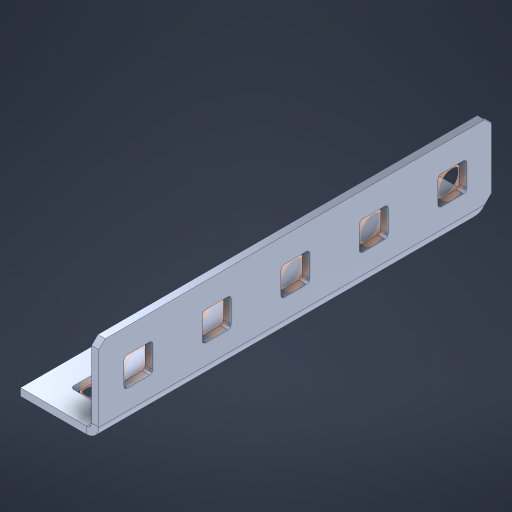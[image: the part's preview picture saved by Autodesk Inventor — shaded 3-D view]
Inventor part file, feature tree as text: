
AUTODESK INVENTOR PART (.ipt)
format: ipt  version: 2023 (Build 270158000, 158)  size: 450,560 bytes
history: native  units: in
note: dims shown in document units (in); Inventor stores cm internally (conversion verified against a paired STEP export)
features: other x15, sheet_metal_op x10, extrude x9, sketch x8, mirror x1, pattern_linear x1, chamfer x1
ambient origin geometry x8: Origin, YZ Plane, XZ Plane, XY Plane, X Axis, Y Axis, Z Axis, Center Point
bodies: Solid1 (feature_tree), Body (feature_tree)
feature tree (45):
  other  "Flange Pattern Plane"
  sheet_metal_op  "Flange Pattern"
  sheet_metal_op  "Body Pattern"
  other  "Arc Length"
  mirror  "Notch Mirror"
  pattern_linear  "Notch Pattern"  Spacing1=0.1875in  [1 undecoded]
  chamfer  "End Chamfer"
  extrude  "Half Cut"  Depth=0.0469in
  sketch  "Sketch1"  dims[d0=2.5in]
  other  "Plate1"
  sketch  "Sketch2"  dims[d1=2.5in]
  other  "Plate2"
  sheet_metal_op  "Bend1"
  sheet_metal_op  "Corner1"
  sketch  "Sketch3"  dims[d2=0.0469in]
  other  "Flange Pattern Sketch"
  sketch  "Sketch7"  dims[d3=0.0469in]
  other  "Srf1"
  other  "Srf2"
  sketch  "Sketch8"  dims[d4=0.0234in]
  sketch  "Sketch9"  dims[d5=0.0938in]
  other  "Srf91"
  sheet_metal_op  "Body Pattern Sketch"
  other  "Srf92"
  sketch  "Sketch13"  dims[d6=0.0469in]
  sketch  "Sketch14"  dims[d7=0.5in d8=90.0deg d9=0.0312in d10=0.1875in d11=0.0469in d12=0.0469in d16=0.182in d17=0.02in d18=0.0469in d19=0.0in d20=0.25in d21=0.25in d46=0.172in d47=1.0in d48=0.0in d49=0.182in d50=0.02in d51=0.25in d52=0.25in d53=0.0469in d54=0.0in d55=0.172in d56=1.0in d57=0.0in d60=1.9685in d62=0.5in d63=0.3937in d65=0.5in d85=0.1227in d86=0.1659in d88=0.04in d89=0.0469in d90=0.0in d91=0.04in d92=0.0491in d95=2.5in d96=0.04in d97=0.25in d98=45.0deg d101=0.0in d102=2.497in d131=0.5in d132=1.9685in d134=0.5in d139=0.5in]
  other  "Srf856"
  other  "Srf1310"
  other  "Srf1311"
  other  "Srf1312"
  other  "Srf1376"
  other  "Srf1377"
  sheet_metal_op  "Flange Stamp"
  sheet_metal_op  "Flange Circle"
  sheet_metal_op  "Body Stamp"
  sheet_metal_op  "Body Circle"
  sheet_metal_op  "Notch"
  extrude  "ExtrusionSrf2"  Depth=0.0469in
  extrude  "ExtrusionSrf92"  Depth=0.5in
  extrude  "ExtrusionSrf856"  Depth=0.02in
  extrude  "ExtrusionSrf1310"  Depth=0.0469in
  extrude  "ExtrusionSrf1311"  TaperAngle=0.0deg  [1 undecoded]
  extrude  "ExtrusionSrf1312"  Depth=0.5in
  extrude  "ExtrusionSrf1376"  Depth=0.5in
  extrude  "ExtrusionSrf1377"  Depth=0.5in
note: 2 required parameter values undecoded (feature->parameter linkage not recoverable at this tier; creation-order binding heuristic only, values carry confidence <= 0.55)
